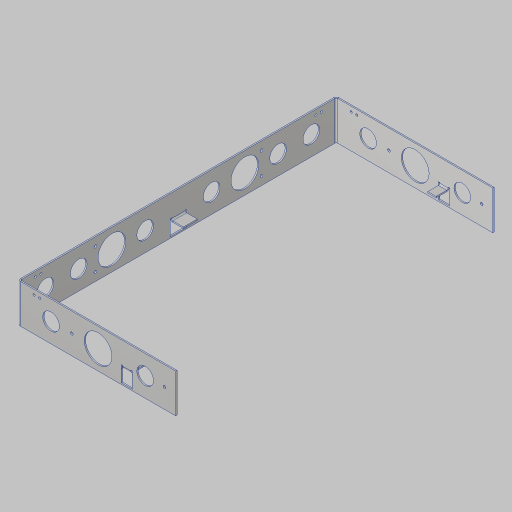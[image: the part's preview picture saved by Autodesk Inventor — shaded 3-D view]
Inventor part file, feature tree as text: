
AUTODESK INVENTOR PART (.ipt)
format: ipt  version: 2023.5 (Build 275446000, 446)  size: 439,808 bytes
history: native  units: in
note: dims shown in document units (in); Inventor stores cm internally (conversion verified against a paired STEP export)
features: sketch x13, sheet_metal_op x10, other x9, projected_geometry x7, hole x4, plane x1, mirror x1
ambient origin geometry x8: Origin, YZ Plane, XZ Plane, XY Plane, X Axis, Y Axis, Z Axis, Center Point
bodies: Solid1 (feature_tree)
feature tree (45):
  sheet_metal_op  "Face1"
  sheet_metal_op  "Flange1"
  hole  "Hole1"  [1 undecoded]
  hole  "Hole2"  [1 undecoded]
  sketch  "Sketch7"  dims[d12=0.12in]
  hole  "Hole3"  [1 undecoded]
  hole  "Hole4"  [1 undecoded]
  sheet_metal_op  "Flange2"
  sheet_metal_op  "Flange3"
  plane  "Work Plane1"
  mirror  "Mirror1"
  sketch  "Sketch1"  dims[d0=3.5in d1=28.75in]
  other  "Plate1"
  sketch  "Sketch2"  dims[d2=0.12in d3=0.12in]
  other  "Plate2"
  sheet_metal_op  "Bend1"
  sheet_metal_op  "Corner1"
  sketch  "Sketch3"  dims[d4=0.06in d5=0.24in]
  sketch  "Sketch4"  dims[d6=0.12in d7=14.25in d8=90.0deg d9=0.12in]
  sketch  "Sketch5"  dims[d10=0.48in]
  sketch  "Sketch6"  dims[d11=0.12in]
  sketch  "Sketch8"  dims[d13=2.5in]
  projected_geometry  "Projected Loop1"
  sketch  "Sketch9"  dims[d14=1.5in]
  projected_geometry  "Projected Loop2"
  sketch  "Sketch10"  dims[d15=3.0in]
  sketch  "Sketch11"  dims[d16=3.0in]
  other  "Plate3"
  sheet_metal_op  "Bend2"
  sheet_metal_op  "Corner2"
  sketch  "Sketch12"  dims[d17=3.0in]
  sketch  "Sketch13"  dims[d19=0.12in d20=0.0in d21=2.5in d22=1.5in d23=1.5in d24=4.25in d25=4.25in d26=0.12in d27=0.0in d28=2.0in d29=7.5in d30=0.25in d31=0.75in d32=0.119in d33=0.25in d34=0.5635in d35=0.12in d36=0.8108in d38=6.0in d39=0.25in d40=0.75in d41=0.375in d42=0.25in d43=0.5635in d44=1.0in d45=0.8108in d47=0.5in d49=0.438in d50=0.201in d51=0.75in d52=0.385in d53=0.25in d54=0.5635in d55=0.12in d56=0.8108in d57=0.5in d59=1.341in d60=0.438in d61=0.201in d62=0.75in d63=0.375in d64=0.25in d65=0.5635in d66=1.0in d67=0.8108in d68=1.341in d69=2.2505in d70=1.5in d71=1.125in d72=0.12in d73=0.0in d74=0.12in d75=0.06in d76=0.24in d77=0.12in d78=1.2in d79=90.0deg d80=0.12in d81=0.48in d82=0.12in d83=0.12in d84=2.2505in d85=1.125in d86=1.0in d87=0.12in d88=0.0in d89=0.12in d90=0.06in d91=0.24in d92=0.12in d93=1.2in d94=90.0deg d95=0.12in d96=0.48in d97=0.12in d98=0.12in d99=1.5in d100=3.0in d101=0.75in d102=1.25in d104=9.5936in]
  other  "Plate4"
  sheet_metal_op  "Bend3"
  sheet_metal_op  "Corner3"
  projected_geometry  "Projected Loop3"
  other  "Cut1"
  other  "Cut2"
  other  "Cut3"
  other  "Cut4"
  projected_geometry  "Project Cut Edges1"
  projected_geometry  "Project Cut Edges2"
  other  "Definition1"
  projected_geometry  "Project Cut Edges3"
  projected_geometry  "Project Cut Edges4"
note: 4 required parameter values undecoded (feature->parameter linkage not recoverable at this tier; creation-order binding heuristic only, values carry confidence <= 0.55)
